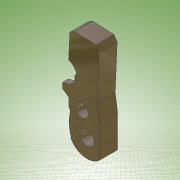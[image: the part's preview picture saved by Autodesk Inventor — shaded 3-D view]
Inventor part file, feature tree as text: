
AUTODESK INVENTOR PART (.ipt)
format: ipt  version: 2011 (Build 150239000, 239)  size: 145,408 bytes
history: native  units: in
note: dims shown in document units (in); Inventor stores cm internally (conversion verified against a paired STEP export)
features: extrude x2, sketch x2, plane x1
ambient origin geometry x8: Origin, YZ Plane, XZ Plane, XY Plane, X Axis, Y Axis, Z Axis, Center Point
bodies: Solid1 (feature_tree)
feature tree (5):
  extrude  "Extrusion1"  Depth=0.275in TaperAngle=0.0deg
  plane  "Work Plane1"
  extrude  "Extrusion2"  Depth=0.1in TaperAngle=0.0deg
  sketch  "Sketch1"  dims[d19=1.0in d23=0.275in d24=0.0in]
  sketch  "Sketch2"  dims[d25=-0.1375in d26=0.1in d27=0.0in]
